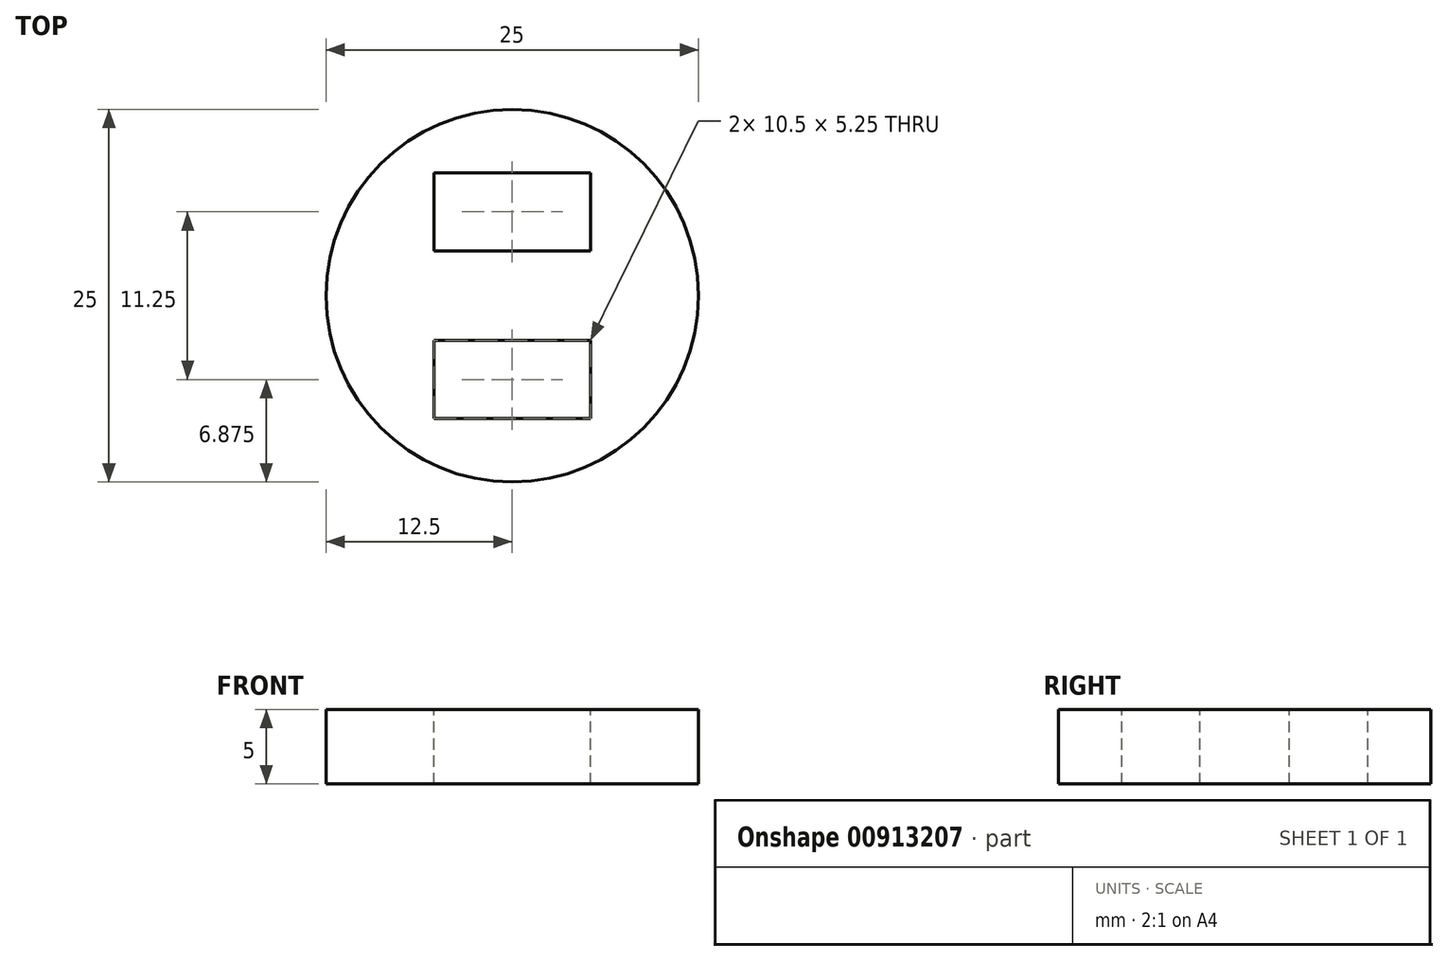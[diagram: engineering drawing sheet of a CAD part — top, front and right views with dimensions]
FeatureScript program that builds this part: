
annotation { "Feature Type Name" : "Feature", "Feature Type Description" : "" }
export const myFeature = defineFeature(function(context is Context, id is Id, definition is map)
    precondition{}
    {
        {
            var Q0;
            Q0=qCreatedBy(makeId("Top.planeOp"),FACE);
            var sketch = newSketch(context, id + "F0", { "sketchPlane" : qUnion([Q0])});
            skCircle(sketch, "E0", {"center": v(0, 0) * mm, "radius": 12.5 * mm});
            skSolve(sketch);
        }
        {
            var Q0;
            Q0 = qSketchRegion(id + "F0", true);
            extrude(context, id + "F1", {"entities" : qUnion([Q0]), "depth" : 5 * mm, "offsetDistance" : 25 * mm});
        }
        {
            var Q0;
            Q0=makeQuery(id+"F1.opExtrude","CAP_FACE",FACE,{"disambiguationData":[OSD([sQuery(id+"F0.wireOp",EDGE,"E0")])],"isStart":false});
            var sketch = newSketch(context, id + "F2", { "sketchPlane" : qUnion([Q0])});
            skLineSegment(sketch, "E1.bottom", {"start": v(5.25, 8.25) * mm, "end": v(-5.25, 8.25) * mm});
            skLineSegment(sketch, "E1.top", {"start": v(5.25, 3) * mm, "end": v(-5.25, 3) * mm});
            skLineSegment(sketch, "E1.left", {"start": v(5.25, 8.25) * mm, "end": v(5.25, 3) * mm});
            skLineSegment(sketch, "E1.right", {"start": v(-5.25, 8.25) * mm, "end": v(-5.25, 3) * mm});
            skPoint(sketch, "E1.middle", {"position": v(0, 5.62) * mm});
            skLineSegment(sketch, "E2.bottom", {"start": v(5.25, -3) * mm, "end": v(-5.25, -3) * mm});
            skLineSegment(sketch, "E2.top", {"start": v(5.25, -8.25) * mm, "end": v(-5.25, -8.25) * mm});
            skLineSegment(sketch, "E2.left", {"start": v(5.25, -3) * mm, "end": v(5.25, -8.25) * mm});
            skLineSegment(sketch, "E2.right", {"start": v(-5.25, -3) * mm, "end": v(-5.25, -8.25) * mm});
            skPoint(sketch, "E2.middle", {"position": v(0, -5.62) * mm});
            skCircle(sketch, "E3", {"center": v(0, 0) * mm, "radius": 10 * mm});
            skSolve(sketch);
        }
        {
            var Q0;
            Q0=makeQuery(id+"F2.imprint","IMPRINT",FACE,{"disambiguationData":[TD([[makeQuery(id+"F2.imprint","IMPRINT",EDGE,{"derivedFrom":sQuery(id+"F2.wireOp",EDGE,"E1.bottom")}),1.0]])]});
            var Q1;
            Q1=makeQuery(id+"F2.imprint","IMPRINT",FACE,{"disambiguationData":[TD([[makeQuery(id+"F2.imprint","IMPRINT",EDGE,{"derivedFrom":sQuery(id+"F2.wireOp",EDGE,"E2.bottom")}),1.0]])]});
            extrude(context, id + "F3", {"entities" : qUnion([Q0, Q1]), "depth" : -5 * mm, "offsetDistance" : 25 * mm});
        }
        {
            var Q0;
            Q0=makeQuery(id+"F3.opExtrude","SWEPT_BODY",BODY,{"disambiguationData":[OSD([sQuery(id+"F2.wireOp",EDGE,"E2.bottom"),sQuery(id+"F2.wireOp",EDGE,"E2.top"),sQuery(id+"F2.wireOp",EDGE,"E2.left"),sQuery(id+"F2.wireOp",EDGE,"E2.right")])]});
            var Q1;
            Q1=makeQuery(id+"F3.opExtrude","SWEPT_BODY",BODY,{"disambiguationData":[OSD([sQuery(id+"F2.wireOp",EDGE,"E1.bottom"),sQuery(id+"F2.wireOp",EDGE,"E1.top"),sQuery(id+"F2.wireOp",EDGE,"E1.left"),sQuery(id+"F2.wireOp",EDGE,"E1.right")])]});
            var Q2;
            Q2=makeQuery(id+"F1.opExtrude","SWEPT_BODY",BODY,{"disambiguationData":[OSD([sQuery(id+"F0.wireOp",EDGE,"E0")])]});
            booleanBodies(context, id + "F4", {"operationType" : BooleanOperationType.SUBTRACTION, "tools" : qUnion([Q0, Q1]), "targets" : qUnion([Q2])});
        }
    });
